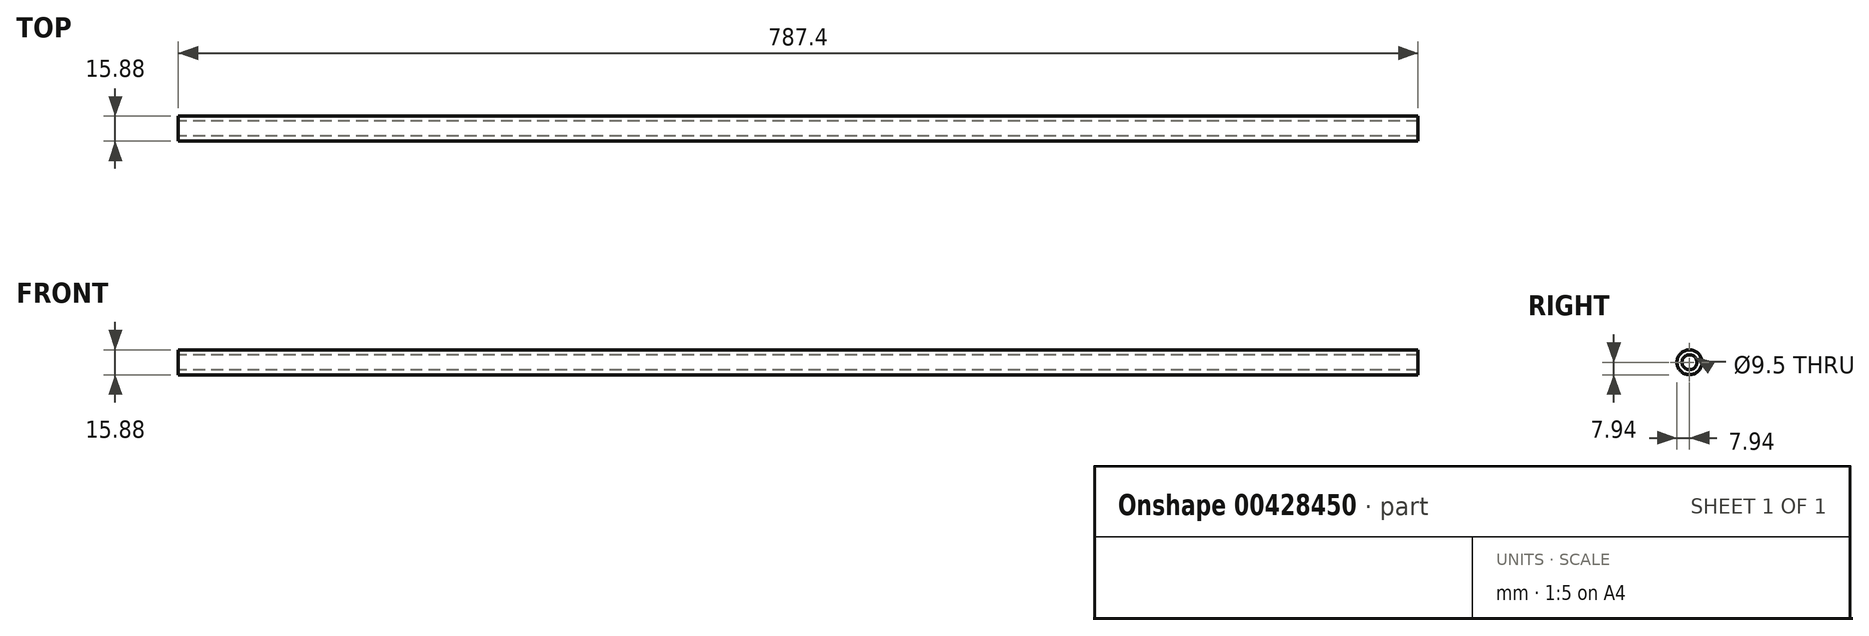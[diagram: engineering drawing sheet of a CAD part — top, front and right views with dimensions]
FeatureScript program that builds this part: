
annotation { "Feature Type Name" : "Feature", "Feature Type Description" : "" }
export const myFeature = defineFeature(function(context is Context, id is Id, definition is map)
    precondition{}
    {
        {
            var Q0;
            Q0=qCreatedBy(makeId("Right.planeOp"),FACE);
            var sketch = newSketch(context, id + "F0", { "sketchPlane" : qUnion([Q0])});
            skCircle(sketch, "E0", {"center": v(0, 0) * mm, "radius": 7.94 * mm});
            skCircle(sketch, "E1", {"center": v(0, 0) * mm, "radius": 4.75 * mm});
            skSolve(sketch);
        }
        {
            var Q0;
            Q0=makeQuery(id+"F0.imprint","IMPRINT",FACE,{"disambiguationData":[TD([[makeQuery(id+"F0.imprint","IMPRINT",EDGE,{"derivedFrom":sQuery(id+"F0.wireOp",EDGE,"E0")}),1.0]])]});
            extrude(context, id + "F1", {"entities" : qUnion([Q0]), "depth" : 393.7 * mm, "hasSecondDirection" : true, "secondDirectionOppositeDirection" : true, "secondDirectionDepth" : 393.7 * mm});
        }
    });
